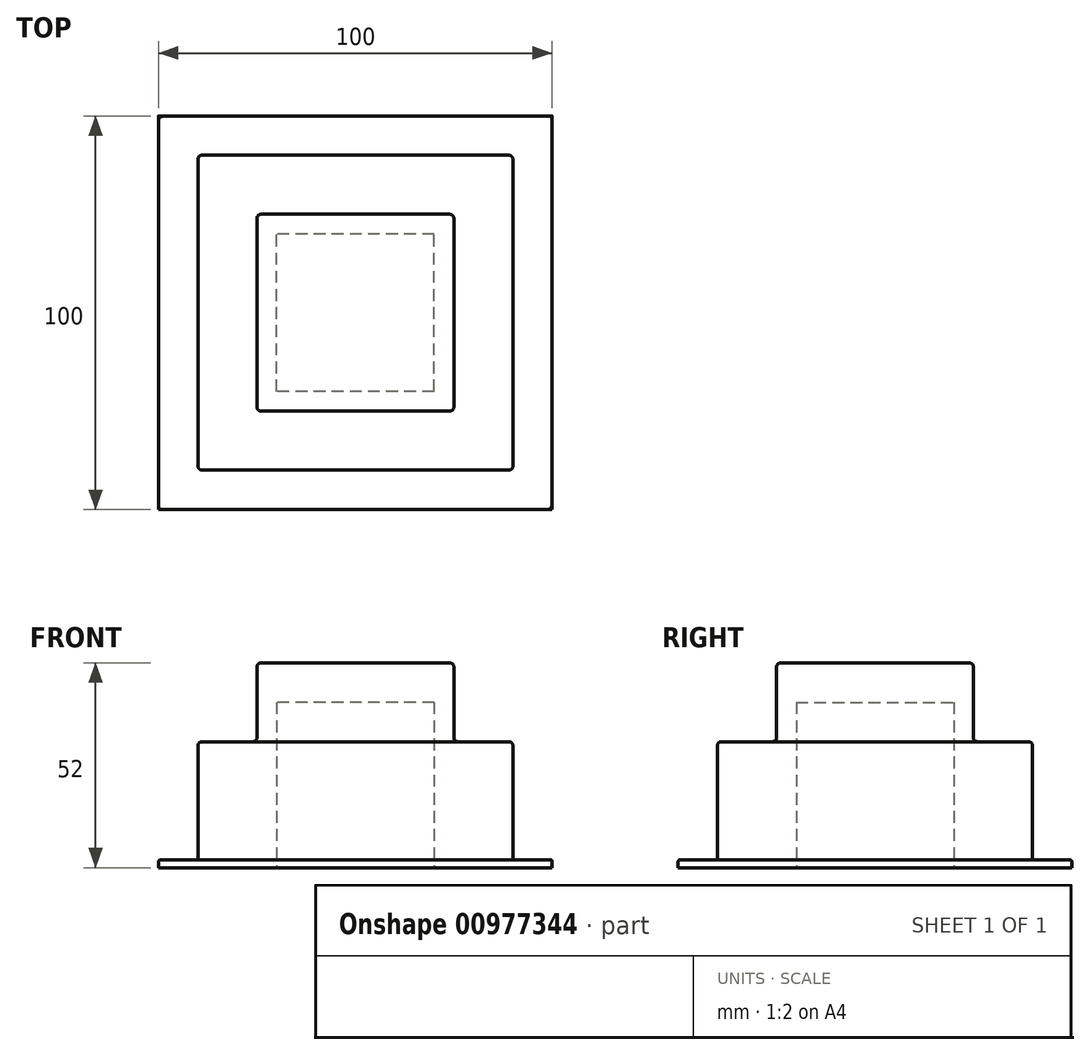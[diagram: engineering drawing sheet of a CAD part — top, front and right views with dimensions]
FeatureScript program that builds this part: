
annotation { "Feature Type Name" : "Feature", "Feature Type Description" : "" }
export const myFeature = defineFeature(function(context is Context, id is Id, definition is map)
    precondition{}
    {
        {
            var Q0;
            Q0=qCreatedBy(makeId("Top.planeOp"),FACE);
            var sketch = newSketch(context, id + "F0", { "sketchPlane" : qUnion([Q0])});
            skLineSegment(sketch, "E0.bottom", {"start": v(50, 50) * mm, "end": v(-50, 50) * mm});
            skLineSegment(sketch, "E0.top", {"start": v(50, -50) * mm, "end": v(-50, -50) * mm});
            skLineSegment(sketch, "E0.left", {"start": v(50, 50) * mm, "end": v(50, -50) * mm});
            skLineSegment(sketch, "E0.right", {"start": v(-50, 50) * mm, "end": v(-50, -50) * mm});
            skPoint(sketch, "E0.middle", {"position": v(0, 0) * mm});
            skSolve(sketch);
        }
        {
            var Q0;
            Q0=makeQuery(id+"F0.imprint","IMPRINT",FACE,{"disambiguationData":[TD([[makeQuery(id+"F0.imprint","IMPRINT",EDGE,{"derivedFrom":sQuery(id+"F0.wireOp",EDGE,"E0.bottom")}),1.0]])]});
            extrude(context, id + "F1", {"entities" : qUnion([Q0]), "depth" : 2 * mm, "offsetDistance" : 25 * mm});
        }
        {
            var Q0;
            Q0=makeQuery(id+"F1.opExtrude","CAP_FACE",FACE,{"disambiguationData":[OSD([sQuery(id+"F0.wireOp",EDGE,"E0.bottom"),sQuery(id+"F0.wireOp",EDGE,"E0.top"),sQuery(id+"F0.wireOp",EDGE,"E0.left"),sQuery(id+"F0.wireOp",EDGE,"E0.right")])],"isStart":false});
            fillet(context, id + "F2", {"entities" : qUnion([Q0]), "radius" : .5 * mm, "tangentPropagation" : true, "allowEdgeOverflow" : false});
        }
        {
            var Q0;
            Q0=makeQuery(id+"F1.opExtrude","CAP_FACE",FACE,{"disambiguationData":[OSD([sQuery(id+"F0.wireOp",EDGE,"E0.bottom"),sQuery(id+"F0.wireOp",EDGE,"E0.top"),sQuery(id+"F0.wireOp",EDGE,"E0.left"),sQuery(id+"F0.wireOp",EDGE,"E0.right")])],"isStart":false});
            cPlane(context, id + "F3", {"entities" : qUnion([Q0]), "cplaneType" : CPlaneType.OFFSET, "offset" : 0 * mm, "width" : 150 * mm, "height" : 150 * mm});
        }
        {
            var Q0;
            Q0=qCreatedBy(id+"F3.planeOp",FACE);
            var sketch = newSketch(context, id + "F4", { "sketchPlane" : qUnion([Q0])});
            skLineSegment(sketch, "E1.bottom", {"start": v(40, 40) * mm, "end": v(-40, 40) * mm});
            skLineSegment(sketch, "E1.top", {"start": v(40, -40) * mm, "end": v(-40, -40) * mm});
            skLineSegment(sketch, "E1.left", {"start": v(40, 40) * mm, "end": v(40, -40) * mm});
            skLineSegment(sketch, "E1.right", {"start": v(-40, 40) * mm, "end": v(-40, -40) * mm});
            skPoint(sketch, "E1.middle", {"position": v(0, 0) * mm});
            skSolve(sketch);
        }
        {
            var Q0;
            Q0=makeQuery(id+"F4.imprint","IMPRINT",FACE,{"disambiguationData":[TD([[makeQuery(id+"F4.imprint","IMPRINT",EDGE,{"derivedFrom":sQuery(id+"F4.wireOp",EDGE,"E1.bottom")}),1.0]])]});
            extrude(context, id + "F5", {"entities" : qUnion([Q0]), "operationType" : NewBodyOperationType.ADD, "depth" : 30 * mm, "offsetDistance" : 25 * mm});
        }
        {
            var Q0;
            Q0=makeQuery(id+"F5.opExtrude","SWEPT_EDGE",EDGE,{"disambiguationData":[OSD([sQuery(id+"F4.wireOp",EDGE,"E1.top"),sQuery(id+"F4.wireOp",EDGE,"E1.right")])]});
            var Q1;
            Q1=makeQuery(id+"F5.opExtrude","SWEPT_EDGE",EDGE,{"disambiguationData":[OSD([sQuery(id+"F4.wireOp",EDGE,"E1.top"),sQuery(id+"F4.wireOp",EDGE,"E1.left")])]});
            var Q2;
            Q2=makeQuery(id+"F5.opExtrude","SWEPT_EDGE",EDGE,{"disambiguationData":[OSD([sQuery(id+"F4.wireOp",EDGE,"E1.bottom"),sQuery(id+"F4.wireOp",EDGE,"E1.left")])]});
            var Q3;
            Q3=makeQuery(id+"F5.opExtrude","SWEPT_EDGE",EDGE,{"disambiguationData":[OSD([sQuery(id+"F4.wireOp",EDGE,"E1.bottom"),sQuery(id+"F4.wireOp",EDGE,"E1.right")])]});
            fillet(context, id + "F6", {"entities" : qUnion([Q0, Q1, Q2, Q3]), "radius" : 1 * mm, "tangentPropagation" : true, "allowEdgeOverflow" : false});
        }
        {
            var Q0;
            Q0=makeQuery(id+"F5.opExtrude","CAP_FACE",FACE,{"disambiguationData":[OSD([sQuery(id+"F4.wireOp",EDGE,"E1.bottom"),sQuery(id+"F4.wireOp",EDGE,"E1.top"),sQuery(id+"F4.wireOp",EDGE,"E1.left"),sQuery(id+"F4.wireOp",EDGE,"E1.right")])],"isStart":false});
            fillet(context, id + "F7", {"entities" : qUnion([Q0]), "radius" : 1 * mm, "tangentPropagation" : true, "allowEdgeOverflow" : false});
        }
        {
            var Q0;
            Q0=makeQuery(id+"F5.opExtrude","CAP_FACE",FACE,{"disambiguationData":[OSD([sQuery(id+"F4.wireOp",EDGE,"E1.bottom"),sQuery(id+"F4.wireOp",EDGE,"E1.top"),sQuery(id+"F4.wireOp",EDGE,"E1.left"),sQuery(id+"F4.wireOp",EDGE,"E1.right")])],"isStart":false});
            var sketch = newSketch(context, id + "F8", { "sketchPlane" : qUnion([Q0])});
            skLineSegment(sketch, "E2.bottom", {"start": v(25, 25) * mm, "end": v(-25, 25) * mm});
            skLineSegment(sketch, "E2.top", {"start": v(25, -25) * mm, "end": v(-25, -25) * mm});
            skLineSegment(sketch, "E2.left", {"start": v(25, 25) * mm, "end": v(25, -25) * mm});
            skLineSegment(sketch, "E2.right", {"start": v(-25, 25) * mm, "end": v(-25, -25) * mm});
            skPoint(sketch, "E2.middle", {"position": v(0, 0) * mm});
            skSolve(sketch);
        }
        {
            var Q0;
            Q0 = qSketchRegion(id + "F8", true);
            extrude(context, id + "F9", {"entities" : qUnion([Q0]), "operationType" : NewBodyOperationType.ADD, "depth" : 20 * mm, "offsetDistance" : 25 * mm});
        }
        {
            var Q0;
            Q0=makeQuery(id+"F9.opExtrude","SWEPT_FACE",FACE,{"disambiguationData":[OSD([sQuery(id+"F8.wireOp",EDGE,"E2.top")])]});
            var Q1;
            Q1=makeQuery(id+"F9.opExtrude","SWEPT_FACE",FACE,{"disambiguationData":[OSD([sQuery(id+"F8.wireOp",EDGE,"E2.right")])]});
            var Q2;
            Q2=makeQuery(id+"F9.opExtrude","CAP_FACE",FACE,{"disambiguationData":[OSD([sQuery(id+"F8.wireOp",EDGE,"E2.bottom"),sQuery(id+"F8.wireOp",EDGE,"E2.top"),sQuery(id+"F8.wireOp",EDGE,"E2.left"),sQuery(id+"F8.wireOp",EDGE,"E2.right")])],"isStart":false});
            var Q3;
            Q3=makeQuery(id+"F9.opExtrude","SWEPT_FACE",FACE,{"disambiguationData":[OSD([sQuery(id+"F8.wireOp",EDGE,"E2.left")])]});
            var Q4;
            Q4=makeQuery(id+"F9.opExtrude","SWEPT_FACE",FACE,{"disambiguationData":[OSD([sQuery(id+"F8.wireOp",EDGE,"E2.bottom")])]});
            fillet(context, id + "F10", {"entities" : qUnion([Q0, Q1, Q2, Q3, Q4]), "radius" : 1 * mm, "tangentPropagation" : true, "allowEdgeOverflow" : false});
        }
        {
            var Q0;
            Q0=makeQuery(id+"F1.opExtrude","CAP_FACE",FACE,{"disambiguationData":[OSD([sQuery(id+"F0.wireOp",EDGE,"E0.bottom"),sQuery(id+"F0.wireOp",EDGE,"E0.top"),sQuery(id+"F0.wireOp",EDGE,"E0.left"),sQuery(id+"F0.wireOp",EDGE,"E0.right")])],"isStart":true});
            var sketch = newSketch(context, id + "F11", { "sketchPlane" : qUnion([Q0])});
            skLineSegment(sketch, "E3.bottom", {"start": v(20, 20) * mm, "end": v(-20, 20) * mm});
            skLineSegment(sketch, "E3.top", {"start": v(20, -20) * mm, "end": v(-20, -20) * mm});
            skLineSegment(sketch, "E3.left", {"start": v(20, 20) * mm, "end": v(20, -20) * mm});
            skLineSegment(sketch, "E3.right", {"start": v(-20, 20) * mm, "end": v(-20, -20) * mm});
            skPoint(sketch, "E3.middle", {"position": v(0, 0) * mm});
            skSolve(sketch);
        }
        {
            var Q0;
            Q0=makeQuery(id+"F11.imprint","IMPRINT",FACE,{"disambiguationData":[TD([[makeQuery(id+"F11.imprint","IMPRINT",EDGE,{"derivedFrom":sQuery(id+"F11.wireOp",EDGE,"E3.bottom")}),1.0]])]});
            extrude(context, id + "F12", {"entities" : qUnion([Q0]), "operationType" : NewBodyOperationType.REMOVE, "oppositeDirection" : true, "depth" : 42 * mm, "offsetDistance" : 25 * mm});
        }
    });
